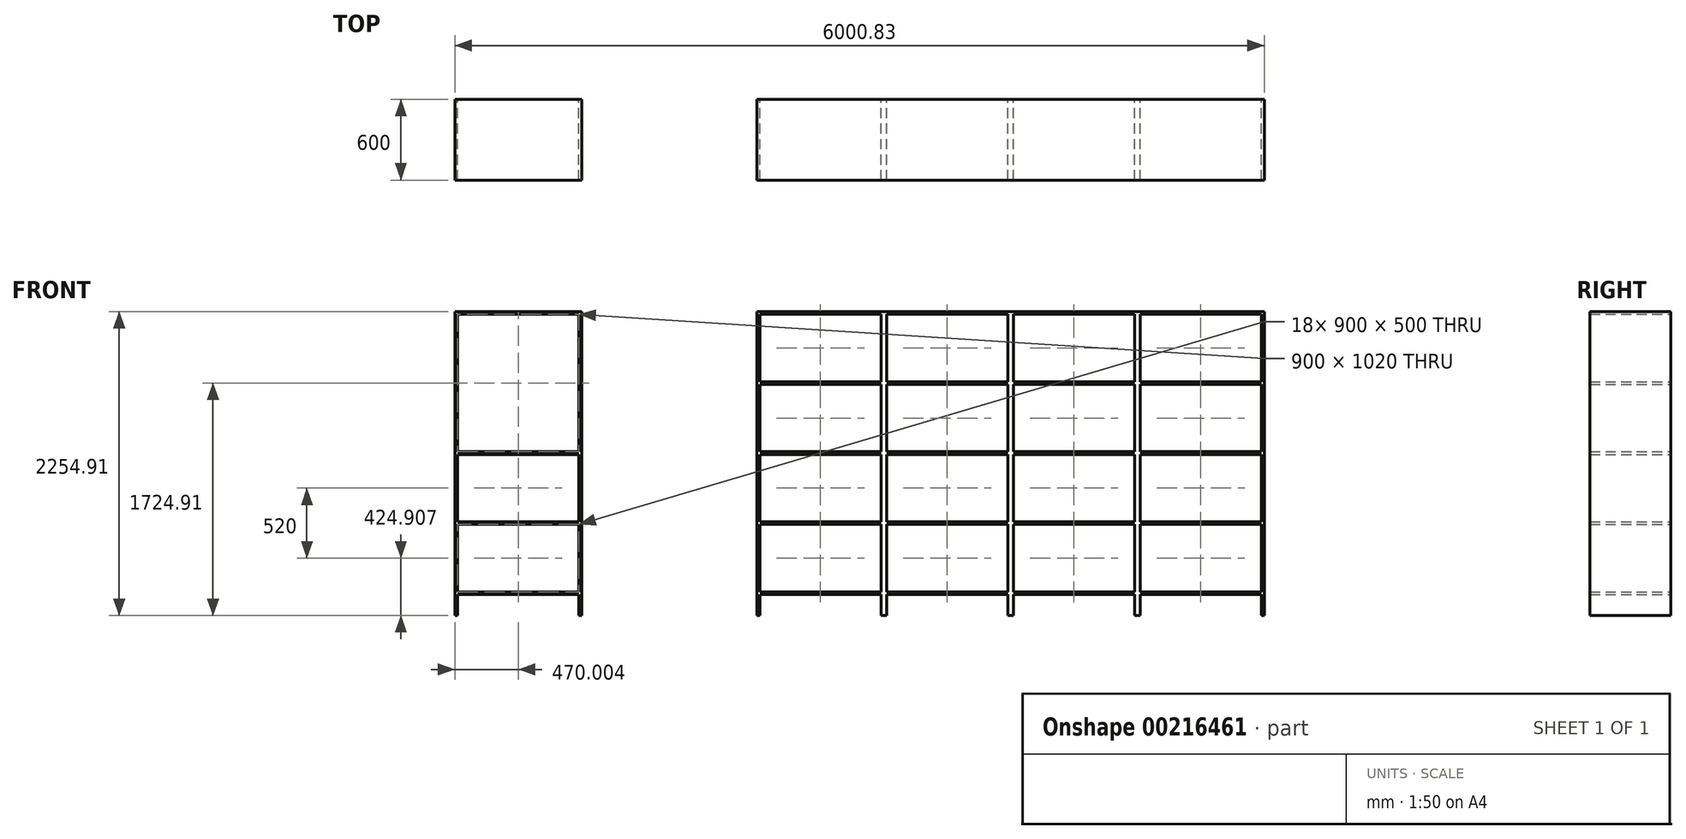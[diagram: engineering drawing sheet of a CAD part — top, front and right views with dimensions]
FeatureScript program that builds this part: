
annotation { "Feature Type Name" : "Feature", "Feature Type Description" : "" }
export const myFeature = defineFeature(function(context is Context, id is Id, definition is map)
    precondition{}
    {
        {
            var Q0;
            Q0=qCreatedBy(makeId("Front.planeOp"),FACE);
            var sketch = newSketch(context, id + "F0", { "sketchPlane" : qUnion([Q0])});
            skLineSegment(sketch, "E0.bottom", {"start": v(0, 842.8) * mm, "end": v(900, 842.8) * mm});
            skLineSegment(sketch, "E0.top", {"start": v(0, 342.8) * mm, "end": v(900, 342.8) * mm});
            skLineSegment(sketch, "E0.left", {"start": v(0, 842.8) * mm, "end": v(0, 342.8) * mm});
            skLineSegment(sketch, "E0.right", {"start": v(900, 842.8) * mm, "end": v(900, 342.8) * mm});
            skLineSegment(sketch, "E1.top", {"start": v(0, 862.8) * mm, "end": v(900, 862.8) * mm});
            skLineSegment(sketch, "E1.left", {"start": v(0, 842.8) * mm, "end": v(0, 862.8) * mm});
            skLineSegment(sketch, "E1.right", {"start": v(900, 842.8) * mm, "end": v(900, 862.8) * mm});
            skLineSegment(sketch, "E2.top", {"start": v(0, 1362.8) * mm, "end": v(900, 1362.8) * mm});
            skLineSegment(sketch, "E2.left", {"start": v(0, 862.8) * mm, "end": v(0, 1362.8) * mm});
            skLineSegment(sketch, "E2.right", {"start": v(900, 862.8) * mm, "end": v(900, 1362.8) * mm});
            skLineSegment(sketch, "E3.top", {"start": v(0, 1382.8) * mm, "end": v(900, 1382.8) * mm});
            skLineSegment(sketch, "E3.left", {"start": v(0, 1362.8) * mm, "end": v(0, 1382.8) * mm});
            skLineSegment(sketch, "E3.right", {"start": v(900, 1362.8) * mm, "end": v(900, 1382.8) * mm});
            skLineSegment(sketch, "E4.top", {"start": v(0, 1882.8) * mm, "end": v(900, 1882.8) * mm});
            skLineSegment(sketch, "E4.left", {"start": v(0, 1382.8) * mm, "end": v(0, 1882.8) * mm});
            skLineSegment(sketch, "E4.right", {"start": v(900, 1382.8) * mm, "end": v(900, 1882.8) * mm});
            skLineSegment(sketch, "E5.top", {"start": v(0, 1902.8) * mm, "end": v(900, 1902.8) * mm});
            skLineSegment(sketch, "E5.left", {"start": v(0, 1882.8) * mm, "end": v(0, 1902.8) * mm});
            skLineSegment(sketch, "E5.right", {"start": v(900, 1882.8) * mm, "end": v(900, 1902.8) * mm});
            skLineSegment(sketch, "E6.top", {"start": v(0, 2402.8) * mm, "end": v(900, 2402.8) * mm});
            skLineSegment(sketch, "E6.left", {"start": v(0, 1902.8) * mm, "end": v(0, 2402.8) * mm});
            skLineSegment(sketch, "E6.right", {"start": v(900, 1902.8) * mm, "end": v(900, 2402.8) * mm});
            skLineSegment(sketch, "E7.bottom", {"start": v(0, 2402.8) * mm, "end": v(-20, 2402.8) * mm});
            skLineSegment(sketch, "E7.top", {"start": v(0, 167.9) * mm, "end": v(-20, 167.9) * mm});
            skLineSegment(sketch, "E7.left", {"start": v(0, 2402.8) * mm, "end": v(0, 167.9) * mm});
            skLineSegment(sketch, "E7.right", {"start": v(-20, 2402.8) * mm, "end": v(-20, 167.9) * mm});
            skLineSegment(sketch, "E8.bottom", {"start": v(900, 2402.8) * mm, "end": v(920, 2402.8) * mm});
            skLineSegment(sketch, "E8.top", {"start": v(900, 167.9) * mm, "end": v(920, 167.9) * mm});
            skLineSegment(sketch, "E8.left", {"start": v(900, 2402.8) * mm, "end": v(900, 167.9) * mm});
            skLineSegment(sketch, "E8.right", {"start": v(920, 2402.8) * mm, "end": v(920, 167.9) * mm});
            skLineSegment(sketch, "E9.bottom", {"start": v(-20, 2402.8) * mm, "end": v(920, 2402.8) * mm});
            skLineSegment(sketch, "E9.top", {"start": v(-20, 2422.8) * mm, "end": v(920, 2422.8) * mm});
            skLineSegment(sketch, "E9.left", {"start": v(-20, 2402.8) * mm, "end": v(-20, 2422.8) * mm});
            skLineSegment(sketch, "E9.right", {"start": v(920, 2402.8) * mm, "end": v(920, 2422.8) * mm});
            skLineSegment(sketch, "E10.bottom", {"start": v(0, 322.8) * mm, "end": v(900, 322.8) * mm});
            skLineSegment(sketch, "E10.left", {"start": v(0, 322.8) * mm, "end": v(0, 342.8) * mm});
            skLineSegment(sketch, "E10.right", {"start": v(900, 322.8) * mm, "end": v(900, 342.8) * mm});
            skLineSegment(sketch, "E11", {"start": v(920, 2626.25) * mm, "end": v(920, 3237.78) * mm, "construction": true});
            skLineSegment(sketch, "E12", {"start": v(-670.41, 2612.4) * mm, "end": v(-670.41, 3024.7) * mm, "construction": true});
            skLineSegment(sketch, "E13.MirrorCS", {"start": v(-2240.83, 1362.8) * mm, "end": v(-2240.83, 1382.8) * mm});
            skLineSegment(sketch, "E14.MirrorCS", {"start": v(-2240.83, 842.8) * mm, "end": v(-2240.83, 862.8) * mm});
            skLineSegment(sketch, "E15.MirrorCS", {"start": v(-1340.83, 842.8) * mm, "end": v(-1340.83, 862.8) * mm});
            skLineSegment(sketch, "E16.MirrorCS", {"start": v(-1340.83, 1362.8) * mm, "end": v(-1340.83, 1382.8) * mm});
            skLineSegment(sketch, "E17.MirrorCS", {"start": v(-1340.83, 322.8) * mm, "end": v(-1340.83, 342.8) * mm});
            skLineSegment(sketch, "E18.MirrorCS", {"start": v(-2240.83, 1882.8) * mm, "end": v(-2240.83, 1902.8) * mm});
            skLineSegment(sketch, "E19.MirrorCS", {"start": v(-1340.83, 1882.8) * mm, "end": v(-1340.83, 1902.8) * mm});
            skLineSegment(sketch, "E20.MirrorCS", {"start": v(-2240.83, 322.8) * mm, "end": v(-2240.83, 342.8) * mm});
            skLineSegment(sketch, "E21.MirrorCS", {"start": v(-1340.83, 167.9) * mm, "end": v(-1320.83, 167.9) * mm});
            skLineSegment(sketch, "E22.MirrorCS", {"start": v(-2240.83, 167.9) * mm, "end": v(-2260.83, 167.9) * mm});
            skLineSegment(sketch, "E23.MirrorCS", {"start": v(-2240.83, 1382.8) * mm, "end": v(-2240.83, 1882.8) * mm});
            skLineSegment(sketch, "E24.MirrorCS", {"start": v(-1340.83, 1882.8) * mm, "end": v(-2240.83, 1882.8) * mm});
            skLineSegment(sketch, "E25.MirrorCS", {"start": v(-2240.83, 862.8) * mm, "end": v(-2240.83, 1362.8) * mm});
            skLineSegment(sketch, "E26.MirrorCS", {"start": v(-1340.83, 1902.8) * mm, "end": v(-2240.83, 1902.8) * mm});
            skLineSegment(sketch, "E27.MirrorCS", {"start": v(-1340.83, 842.8) * mm, "end": v(-1340.83, 342.8) * mm});
            skLineSegment(sketch, "E28.MirrorCS", {"start": v(-1340.83, 1382.8) * mm, "end": v(-2240.83, 1382.8) * mm});
            skLineSegment(sketch, "E29.MirrorCS", {"start": v(-1340.83, 1902.8) * mm, "end": v(-1340.83, 2402.8) * mm});
            skLineSegment(sketch, "E30.MirrorCS", {"start": v(-1340.83, 1362.8) * mm, "end": v(-2240.83, 1362.8) * mm});
            skLineSegment(sketch, "E31.MirrorCS", {"start": v(-1340.83, 862.8) * mm, "end": v(-2240.83, 862.8) * mm});
            skLineSegment(sketch, "E32.MirrorCS", {"start": v(-2240.83, 842.8) * mm, "end": v(-2240.83, 342.8) * mm});
            skLineSegment(sketch, "E33.MirrorCS", {"start": v(-1340.83, 862.8) * mm, "end": v(-1340.83, 1362.8) * mm});
            skLineSegment(sketch, "E34.MirrorCS", {"start": v(-2240.83, 1902.8) * mm, "end": v(-2240.83, 2402.8) * mm});
            skLineSegment(sketch, "E35.MirrorCS", {"start": v(-1340.83, 842.8) * mm, "end": v(-2240.83, 842.8) * mm});
            skLineSegment(sketch, "E36.MirrorCS", {"start": v(-1340.83, 342.8) * mm, "end": v(-2240.83, 342.8) * mm});
            skLineSegment(sketch, "E37.MirrorCS", {"start": v(-1340.83, 322.8) * mm, "end": v(-2240.83, 322.8) * mm});
            skLineSegment(sketch, "E38.MirrorCS", {"start": v(-2260.83, 2402.8) * mm, "end": v(-2260.83, 167.9) * mm});
            skLineSegment(sketch, "E39.MirrorCS", {"start": v(-2240.83, 2402.8) * mm, "end": v(-2240.83, 167.9) * mm});
            skLineSegment(sketch, "E40.MirrorCS", {"start": v(-1320.83, 2402.8) * mm, "end": v(-1320.83, 167.9) * mm});
            skLineSegment(sketch, "E41.MirrorCS", {"start": v(-1340.83, 2402.8) * mm, "end": v(-1340.83, 167.9) * mm});
            skLineSegment(sketch, "E42.MirrorCS", {"start": v(-1340.83, 1382.8) * mm, "end": v(-1340.83, 1882.8) * mm});
            skLineSegment(sketch, "E43.MirrorCS", {"start": v(-1340.83, 2402.8) * mm, "end": v(-2240.83, 2402.8) * mm});
            skLineSegment(sketch, "E44.MirrorCS", {"start": v(-1320.83, 2422.8) * mm, "end": v(-2260.83, 2422.8) * mm});
            skLineSegment(sketch, "E45.MirrorCS", {"start": v(1840, 2402.8) * mm, "end": v(1860, 2402.8) * mm});
            skLineSegment(sketch, "E46.MirrorCS", {"start": v(940, 322.8) * mm, "end": v(940, 342.8) * mm});
            skLineSegment(sketch, "E47.MirrorCS", {"start": v(1840, 1362.8) * mm, "end": v(1840, 1382.8) * mm});
            skLineSegment(sketch, "E48.MirrorCS", {"start": v(940, 1362.8) * mm, "end": v(940, 1382.8) * mm});
            skLineSegment(sketch, "E49.MirrorCS", {"start": v(940, 2402.8) * mm, "end": v(920, 2402.8) * mm});
            skLineSegment(sketch, "E50.MirrorCS", {"start": v(1860, 2402.8) * mm, "end": v(1860, 2422.8) * mm});
            skLineSegment(sketch, "E51.MirrorCS", {"start": v(940, 1882.8) * mm, "end": v(940, 1902.8) * mm});
            skLineSegment(sketch, "E52.MirrorCS", {"start": v(940, 842.8) * mm, "end": v(940, 862.8) * mm});
            skLineSegment(sketch, "E53.MirrorCS", {"start": v(1840, 1882.8) * mm, "end": v(1840, 1902.8) * mm});
            skLineSegment(sketch, "E54.MirrorCS", {"start": v(1840, 322.8) * mm, "end": v(1840, 342.8) * mm});
            skLineSegment(sketch, "E55.MirrorCS", {"start": v(1840, 842.8) * mm, "end": v(1840, 862.8) * mm});
            skLineSegment(sketch, "E56.MirrorCS", {"start": v(1840, 167.9) * mm, "end": v(1860, 167.9) * mm});
            skLineSegment(sketch, "E57.MirrorCS", {"start": v(940, 167.9) * mm, "end": v(920, 167.9) * mm});
            skLineSegment(sketch, "E58.MirrorCS", {"start": v(1840, 842.8) * mm, "end": v(940, 842.8) * mm});
            skLineSegment(sketch, "E59.MirrorCS", {"start": v(1840, 342.8) * mm, "end": v(940, 342.8) * mm});
            skLineSegment(sketch, "E60.MirrorCS", {"start": v(1840, 1902.8) * mm, "end": v(940, 1902.8) * mm});
            skLineSegment(sketch, "E61.MirrorCS", {"start": v(940, 1902.8) * mm, "end": v(940, 2402.8) * mm});
            skLineSegment(sketch, "E62.MirrorCS", {"start": v(1840, 1882.8) * mm, "end": v(940, 1882.8) * mm});
            skLineSegment(sketch, "E63.MirrorCS", {"start": v(1840, 1382.8) * mm, "end": v(940, 1382.8) * mm});
            skLineSegment(sketch, "E64.MirrorCS", {"start": v(1860, 2402.8) * mm, "end": v(920, 2402.8) * mm});
            skLineSegment(sketch, "E65.MirrorCS", {"start": v(1840, 862.8) * mm, "end": v(940, 862.8) * mm});
            skLineSegment(sketch, "E66.MirrorCS", {"start": v(940, 862.8) * mm, "end": v(940, 1362.8) * mm});
            skLineSegment(sketch, "E67.MirrorCS", {"start": v(940, 842.8) * mm, "end": v(940, 342.8) * mm});
            skLineSegment(sketch, "E68.MirrorCS", {"start": v(940, 1382.8) * mm, "end": v(940, 1882.8) * mm});
            skLineSegment(sketch, "E69.MirrorCS", {"start": v(1840, 1362.8) * mm, "end": v(940, 1362.8) * mm});
            skLineSegment(sketch, "E70.MirrorCS", {"start": v(1840, 1902.8) * mm, "end": v(1840, 2402.8) * mm});
            skLineSegment(sketch, "E71.MirrorCS", {"start": v(1840, 2402.8) * mm, "end": v(940, 2402.8) * mm});
            skLineSegment(sketch, "E72.MirrorCS", {"start": v(1840, 1382.8) * mm, "end": v(1840, 1882.8) * mm});
            skLineSegment(sketch, "E73.MirrorCS", {"start": v(940, 2402.8) * mm, "end": v(940, 167.9) * mm});
            skLineSegment(sketch, "E74.MirrorCS", {"start": v(1860, 2422.8) * mm, "end": v(920, 2422.8) * mm});
            skLineSegment(sketch, "E75.MirrorCS", {"start": v(1840, 2402.8) * mm, "end": v(1840, 167.9) * mm});
            skLineSegment(sketch, "E76.MirrorCS", {"start": v(1860, 2402.8) * mm, "end": v(1860, 167.9) * mm});
            skLineSegment(sketch, "E77.MirrorCS", {"start": v(1840, 842.8) * mm, "end": v(1840, 342.8) * mm});
            skLineSegment(sketch, "E78.MirrorCS", {"start": v(1840, 862.8) * mm, "end": v(1840, 1362.8) * mm});
            skLineSegment(sketch, "E79.MirrorCS", {"start": v(1840, 322.8) * mm, "end": v(940, 322.8) * mm});
            skLineSegment(sketch, "E80", {"start": v(1860, 2643.35) * mm, "end": v(1860, 2780.12) * mm, "construction": true});
            skLineSegment(sketch, "E81.MirrorCS", {"start": v(2800, 2402.8) * mm, "end": v(2800, 2422.8) * mm});
            skLineSegment(sketch, "E82.MirrorCS", {"start": v(2780, 2402.8) * mm, "end": v(2800, 2402.8) * mm});
            skLineSegment(sketch, "E83.MirrorCS", {"start": v(2820, 2402.8) * mm, "end": v(2800, 2402.8) * mm});
            skLineSegment(sketch, "E84.MirrorCS", {"start": v(3720, 2402.8) * mm, "end": v(3740, 2402.8) * mm});
            skLineSegment(sketch, "E85.MirrorCS", {"start": v(2780, 167.9) * mm, "end": v(2800, 167.9) * mm});
            skLineSegment(sketch, "E86.MirrorCS", {"start": v(2820, 167.9) * mm, "end": v(2800, 167.9) * mm});
            skLineSegment(sketch, "E87.MirrorCS", {"start": v(1880, 2402.8) * mm, "end": v(1860, 2402.8) * mm});
            skLineSegment(sketch, "E88.MirrorCS", {"start": v(3740, 2402.8) * mm, "end": v(3740, 2422.8) * mm});
            skLineSegment(sketch, "E89.MirrorCS", {"start": v(2780, 1362.8) * mm, "end": v(2780, 1382.8) * mm});
            skLineSegment(sketch, "E90.MirrorCS", {"start": v(1880, 1362.8) * mm, "end": v(1880, 1382.8) * mm});
            skLineSegment(sketch, "E91.MirrorCS", {"start": v(2820, 1882.8) * mm, "end": v(2820, 1902.8) * mm});
            skLineSegment(sketch, "E92.MirrorCS", {"start": v(3720, 322.8) * mm, "end": v(3720, 342.8) * mm});
            skLineSegment(sketch, "E93.MirrorCS", {"start": v(1880, 1882.8) * mm, "end": v(1880, 1902.8) * mm});
            skLineSegment(sketch, "E94.MirrorCS", {"start": v(2780, 842.8) * mm, "end": v(2780, 862.8) * mm});
            skLineSegment(sketch, "E95.MirrorCS", {"start": v(3720, 1362.8) * mm, "end": v(3720, 1382.8) * mm});
            skLineSegment(sketch, "E96.MirrorCS", {"start": v(1880, 322.8) * mm, "end": v(1880, 342.8) * mm});
            skLineSegment(sketch, "E97.MirrorCS", {"start": v(1880, 842.8) * mm, "end": v(1880, 862.8) * mm});
            skLineSegment(sketch, "E98.MirrorCS", {"start": v(2780, 322.8) * mm, "end": v(2780, 342.8) * mm});
            skLineSegment(sketch, "E99.MirrorCS", {"start": v(3720, 1882.8) * mm, "end": v(3720, 1902.8) * mm});
            skLineSegment(sketch, "E100.MirrorCS", {"start": v(2780, 1882.8) * mm, "end": v(2780, 1902.8) * mm});
            skLineSegment(sketch, "E101.MirrorCS", {"start": v(2820, 842.8) * mm, "end": v(2820, 862.8) * mm});
            skLineSegment(sketch, "E102.MirrorCS", {"start": v(2820, 1362.8) * mm, "end": v(2820, 1382.8) * mm});
            skLineSegment(sketch, "E103.MirrorCS", {"start": v(2820, 322.8) * mm, "end": v(2820, 342.8) * mm});
            skLineSegment(sketch, "E104.MirrorCS", {"start": v(3720, 842.8) * mm, "end": v(3720, 862.8) * mm});
            skLineSegment(sketch, "E105.MirrorCS", {"start": v(2820, 1382.8) * mm, "end": v(2820, 1882.8) * mm});
            skLineSegment(sketch, "E106.MirrorCS", {"start": v(1880, 167.9) * mm, "end": v(1860, 167.9) * mm});
            skLineSegment(sketch, "E107.MirrorCS", {"start": v(2800, 2402.8) * mm, "end": v(2800, 167.9) * mm});
            skLineSegment(sketch, "E108.MirrorCS", {"start": v(3740, 2402.8) * mm, "end": v(2800, 2402.8) * mm});
            skLineSegment(sketch, "E109.MirrorCS", {"start": v(2820, 1902.8) * mm, "end": v(2820, 2402.8) * mm});
            skLineSegment(sketch, "E110.MirrorCS", {"start": v(3720, 167.9) * mm, "end": v(3740, 167.9) * mm});
            skLineSegment(sketch, "E111.MirrorCS", {"start": v(1860, 2422.8) * mm, "end": v(2800, 2422.8) * mm});
            skLineSegment(sketch, "E112.MirrorCS", {"start": v(1880, 2402.8) * mm, "end": v(2780, 2402.8) * mm});
            skLineSegment(sketch, "E113.MirrorCS", {"start": v(1880, 1882.8) * mm, "end": v(2780, 1882.8) * mm});
            skLineSegment(sketch, "E114.MirrorCS", {"start": v(2820, 842.8) * mm, "end": v(2820, 342.8) * mm});
            skLineSegment(sketch, "E115.MirrorCS", {"start": v(1880, 862.8) * mm, "end": v(2780, 862.8) * mm});
            skLineSegment(sketch, "E116.MirrorCS", {"start": v(1880, 862.8) * mm, "end": v(1880, 1362.8) * mm});
            skLineSegment(sketch, "E117.MirrorCS", {"start": v(3720, 1902.8) * mm, "end": v(3720, 2402.8) * mm});
            skLineSegment(sketch, "E118.MirrorCS", {"start": v(1880, 842.8) * mm, "end": v(2780, 842.8) * mm});
            skLineSegment(sketch, "E119.MirrorCS", {"start": v(3720, 342.8) * mm, "end": v(2820, 342.8) * mm});
            skLineSegment(sketch, "E120.MirrorCS", {"start": v(3720, 1902.8) * mm, "end": v(2820, 1902.8) * mm});
            skLineSegment(sketch, "E121.MirrorCS", {"start": v(3720, 1382.8) * mm, "end": v(2820, 1382.8) * mm});
            skLineSegment(sketch, "E122.MirrorCS", {"start": v(1880, 1382.8) * mm, "end": v(2780, 1382.8) * mm});
            skLineSegment(sketch, "E123.MirrorCS", {"start": v(3720, 862.8) * mm, "end": v(2820, 862.8) * mm});
            skLineSegment(sketch, "E124.MirrorCS", {"start": v(3740, 2422.8) * mm, "end": v(2800, 2422.8) * mm});
            skLineSegment(sketch, "E125.MirrorCS", {"start": v(3720, 1882.8) * mm, "end": v(2820, 1882.8) * mm});
            skLineSegment(sketch, "E126.MirrorCS", {"start": v(1880, 342.8) * mm, "end": v(2780, 342.8) * mm});
            skLineSegment(sketch, "E127.MirrorCS", {"start": v(1880, 1362.8) * mm, "end": v(2780, 1362.8) * mm});
            skLineSegment(sketch, "E128.MirrorCS", {"start": v(2820, 862.8) * mm, "end": v(2820, 1362.8) * mm});
            skLineSegment(sketch, "E129.MirrorCS", {"start": v(3720, 842.8) * mm, "end": v(2820, 842.8) * mm});
            skLineSegment(sketch, "E130.MirrorCS", {"start": v(3720, 1362.8) * mm, "end": v(2820, 1362.8) * mm});
            skLineSegment(sketch, "E131.MirrorCS", {"start": v(1880, 1902.8) * mm, "end": v(2780, 1902.8) * mm});
            skLineSegment(sketch, "E132.MirrorCS", {"start": v(1880, 1382.8) * mm, "end": v(1880, 1882.8) * mm});
            skLineSegment(sketch, "E133.MirrorCS", {"start": v(2820, 2402.8) * mm, "end": v(2820, 167.9) * mm});
            skLineSegment(sketch, "E134.MirrorCS", {"start": v(3720, 1382.8) * mm, "end": v(3720, 1882.8) * mm});
            skLineSegment(sketch, "E135.MirrorCS", {"start": v(1860, 2402.8) * mm, "end": v(2800, 2402.8) * mm});
            skLineSegment(sketch, "E136.MirrorCS", {"start": v(3720, 2402.8) * mm, "end": v(2820, 2402.8) * mm});
            skLineSegment(sketch, "E137.MirrorCS", {"start": v(3720, 322.8) * mm, "end": v(2820, 322.8) * mm});
            skLineSegment(sketch, "E138.MirrorCS", {"start": v(1880, 842.8) * mm, "end": v(1880, 342.8) * mm});
            skLineSegment(sketch, "E139.MirrorCS", {"start": v(3720, 842.8) * mm, "end": v(3720, 342.8) * mm});
            skLineSegment(sketch, "E140.MirrorCS", {"start": v(2780, 2402.8) * mm, "end": v(2780, 167.9) * mm});
            skLineSegment(sketch, "E141.MirrorCS", {"start": v(2780, 842.8) * mm, "end": v(2780, 342.8) * mm});
            skLineSegment(sketch, "E142.MirrorCS", {"start": v(2780, 1902.8) * mm, "end": v(2780, 2402.8) * mm});
            skLineSegment(sketch, "E143.MirrorCS", {"start": v(1880, 1902.8) * mm, "end": v(1880, 2402.8) * mm});
            skLineSegment(sketch, "E144.MirrorCS", {"start": v(3720, 2402.8) * mm, "end": v(3720, 167.9) * mm});
            skLineSegment(sketch, "E145.MirrorCS", {"start": v(3740, 2402.8) * mm, "end": v(3740, 167.9) * mm});
            skLineSegment(sketch, "E146.MirrorCS", {"start": v(2780, 862.8) * mm, "end": v(2780, 1362.8) * mm});
            skLineSegment(sketch, "E147.MirrorCS", {"start": v(1880, 322.8) * mm, "end": v(2780, 322.8) * mm});
            skLineSegment(sketch, "E148.MirrorCS", {"start": v(2780, 1382.8) * mm, "end": v(2780, 1882.8) * mm});
            skLineSegment(sketch, "E149.MirrorCS", {"start": v(3720, 862.8) * mm, "end": v(3720, 1362.8) * mm});
            skLineSegment(sketch, "E150.MirrorCS", {"start": v(1880, 2402.8) * mm, "end": v(1880, 167.9) * mm});
            skLineSegment(sketch, "E151.MirrorCS", {"start": v(-2260.83, 2402.8) * mm, "end": v(-2260.83, 2422.8) * mm});
            skLineSegment(sketch, "E152.MirrorCS", {"start": v(-1320.83, 2402.8) * mm, "end": v(-1320.83, 2422.8) * mm});
            skSolve(sketch);
        }
        {
            var Q0;
            {var subQ9=sQuery(id+"F0.wireOp",EDGE,"E7.top");Q0=makeQuery(id+"F0.imprint","IMPRINT",FACE,{"disambiguationData":[TD([[makeQuery(id+"F0.imprint","IMPRINT",EDGE,{"derivedFrom":subQ9}),-1.0]])]});}
            var Q1;
            {var subQ6=sQuery(id+"F0.wireOp",EDGE,"E85.MirrorCS");Q1=makeQuery(id+"F0.imprint","IMPRINT",FACE,{"disambiguationData":[TD([[makeQuery(id+"F0.imprint","IMPRINT",EDGE,{"derivedFrom":subQ6}),1.0]])]});}
            var Q2;
            {var subQ3=sQuery(id+"F0.wireOp",EDGE,"E106.MirrorCS");Q2=makeQuery(id+"F0.imprint","IMPRINT",FACE,{"disambiguationData":[TD([[makeQuery(id+"F0.imprint","IMPRINT",EDGE,{"derivedFrom":subQ3}),-1.0]])]});}
            var Q3;
            {var subQ0=sQuery(id+"F0.wireOp",EDGE,"E129.MirrorCS");Q3=makeQuery(id+"F0.imprint","IMPRINT",FACE,{"disambiguationData":[TD([[makeQuery(id+"F0.imprint","IMPRINT",EDGE,{"derivedFrom":subQ0}),-1.0]])]});}
            var Q4;
            {var subQ11=sQuery(id+"F0.wireOp",EDGE,"E8.top");Q4=makeQuery(id+"F0.imprint","IMPRINT",FACE,{"disambiguationData":[TD([[makeQuery(id+"F0.imprint","IMPRINT",EDGE,{"derivedFrom":subQ11}),1.0]])]});}
            var Q5;
            {var subQ0=sQuery(id+"F0.wireOp",EDGE,"E65.MirrorCS");Q5=makeQuery(id+"F0.imprint","IMPRINT",FACE,{"disambiguationData":[TD([[makeQuery(id+"F0.imprint","IMPRINT",EDGE,{"derivedFrom":subQ0}),1.0]])]});}
            var Q6;
            {var subQ0=sQuery(id+"F0.wireOp",EDGE,"E122.MirrorCS");Q6=makeQuery(id+"F0.imprint","IMPRINT",FACE,{"disambiguationData":[TD([[makeQuery(id+"F0.imprint","IMPRINT",EDGE,{"derivedFrom":subQ0}),-1.0]])]});}
            var Q7;
            {var subQ0=sQuery(id+"F0.wireOp",EDGE,"E2.top");Q7=makeQuery(id+"F0.imprint","IMPRINT",FACE,{"disambiguationData":[TD([[makeQuery(id+"F0.imprint","IMPRINT",EDGE,{"derivedFrom":subQ0}),1.0]])]});}
            var Q8;
            {var subQ0=sQuery(id+"F0.wireOp",EDGE,"E0.bottom");Q8=makeQuery(id+"F0.imprint","IMPRINT",FACE,{"disambiguationData":[TD([[makeQuery(id+"F0.imprint","IMPRINT",EDGE,{"derivedFrom":subQ0}),1.0]])]});}
            var Q9;
            {var subQ0=sQuery(id+"F0.wireOp",EDGE,"E121.MirrorCS");Q9=makeQuery(id+"F0.imprint","IMPRINT",FACE,{"disambiguationData":[TD([[makeQuery(id+"F0.imprint","IMPRINT",EDGE,{"derivedFrom":subQ0}),1.0]])]});}
            var Q10;
            {var subQ2=sQuery(id+"F0.wireOp",EDGE,"E115.MirrorCS");Q10=makeQuery(id+"F0.imprint","IMPRINT",FACE,{"disambiguationData":[TD([[makeQuery(id+"F0.imprint","IMPRINT",EDGE,{"derivedFrom":subQ2}),-1.0]])]});}
            var Q11;
            {var subQ0=sQuery(id+"F0.wireOp",EDGE,"E69.MirrorCS");Q11=makeQuery(id+"F0.imprint","IMPRINT",FACE,{"disambiguationData":[TD([[makeQuery(id+"F0.imprint","IMPRINT",EDGE,{"derivedFrom":subQ0}),-1.0]])]});}
            var Q12;
            {var subQ3=sQuery(id+"F0.wireOp",EDGE,"E81.MirrorCS");Q12=makeQuery(id+"F0.imprint","IMPRINT",FACE,{"disambiguationData":[TD([[makeQuery(id+"F0.imprint","IMPRINT",EDGE,{"derivedFrom":subQ3}),1.0]])]});}
            var Q13;
            {var subQ1=sQuery(id+"F0.wireOp",EDGE,"E81.MirrorCS");Q13=makeQuery(id+"F0.imprint","IMPRINT",FACE,{"disambiguationData":[TD([[makeQuery(id+"F0.imprint","IMPRINT",EDGE,{"derivedFrom":subQ1}),-1.0]])]});}
            var Q14;
            {var subQ12=sQuery(id+"F0.wireOp",EDGE,"E57.MirrorCS");Q14=makeQuery(id+"F0.imprint","IMPRINT",FACE,{"disambiguationData":[TD([[makeQuery(id+"F0.imprint","IMPRINT",EDGE,{"derivedFrom":subQ12}),-1.0]])]});}
            var Q15;
            {var subQ3=sQuery(id+"F0.wireOp",EDGE,"E86.MirrorCS");Q15=makeQuery(id+"F0.imprint","IMPRINT",FACE,{"disambiguationData":[TD([[makeQuery(id+"F0.imprint","IMPRINT",EDGE,{"derivedFrom":subQ3}),-1.0]])]});}
            var Q16;
            {var subQ8=sQuery(id+"F0.wireOp",EDGE,"E110.MirrorCS");Q16=makeQuery(id+"F0.imprint","IMPRINT",FACE,{"disambiguationData":[TD([[makeQuery(id+"F0.imprint","IMPRINT",EDGE,{"derivedFrom":subQ8}),1.0]])]});}
            var Q17;
            Q17=makeQuery(id+"F0.imprint","IMPRINT",FACE,{"disambiguationData":[TD([[makeQuery(id+"F0.imprint","IMPRINT",EDGE,{"derivedFrom":sQuery(id+"F0.wireOp",EDGE,"E9.top")}),-1.0]])]});
            var Q18;
            {var subQ2=sQuery(id+"F0.wireOp",EDGE,"E9.right");Q18=makeQuery(id+"F0.imprint","IMPRINT",FACE,{"disambiguationData":[TD([[makeQuery(id+"F0.imprint","IMPRINT",EDGE,{"derivedFrom":subQ2}),-1.0]])]});}
            var Q19;
            {var subQ0=sQuery(id+"F0.wireOp",EDGE,"E59.MirrorCS");Q19=makeQuery(id+"F0.imprint","IMPRINT",FACE,{"disambiguationData":[TD([[makeQuery(id+"F0.imprint","IMPRINT",EDGE,{"derivedFrom":subQ0}),1.0]])]});}
            var Q20;
            {var subQ0=sQuery(id+"F0.wireOp",EDGE,"E119.MirrorCS");Q20=makeQuery(id+"F0.imprint","IMPRINT",FACE,{"disambiguationData":[TD([[makeQuery(id+"F0.imprint","IMPRINT",EDGE,{"derivedFrom":subQ0}),1.0]])]});}
            var Q21;
            {var subQ4=sQuery(id+"F0.wireOp",EDGE,"E56.MirrorCS");Q21=makeQuery(id+"F0.imprint","IMPRINT",FACE,{"disambiguationData":[TD([[makeQuery(id+"F0.imprint","IMPRINT",EDGE,{"derivedFrom":subQ4}),1.0]])]});}
            var Q22;
            {var subQ0=sQuery(id+"F0.wireOp",EDGE,"E126.MirrorCS");Q22=makeQuery(id+"F0.imprint","IMPRINT",FACE,{"disambiguationData":[TD([[makeQuery(id+"F0.imprint","IMPRINT",EDGE,{"derivedFrom":subQ0}),-1.0]])]});}
            var Q23;
            Q23=makeQuery(id+"F0.imprint","IMPRINT",FACE,{"disambiguationData":[TD([[makeQuery(id+"F0.imprint","IMPRINT",EDGE,{"derivedFrom":sQuery(id+"F0.wireOp",EDGE,"E10.bottom")}),1.0]])]});
            var Q24;
            {var subQ0=sQuery(id+"F0.wireOp",EDGE,"E4.top");Q24=makeQuery(id+"F0.imprint","IMPRINT",FACE,{"disambiguationData":[TD([[makeQuery(id+"F0.imprint","IMPRINT",EDGE,{"derivedFrom":subQ0}),1.0]])]});}
            var Q25;
            {var subQ0=sQuery(id+"F0.wireOp",EDGE,"E113.MirrorCS");Q25=makeQuery(id+"F0.imprint","IMPRINT",FACE,{"disambiguationData":[TD([[makeQuery(id+"F0.imprint","IMPRINT",EDGE,{"derivedFrom":subQ0}),1.0]])]});}
            var Q26;
            {var subQ0=sQuery(id+"F0.wireOp",EDGE,"E125.MirrorCS");Q26=makeQuery(id+"F0.imprint","IMPRINT",FACE,{"disambiguationData":[TD([[makeQuery(id+"F0.imprint","IMPRINT",EDGE,{"derivedFrom":subQ0}),-1.0]])]});}
            var Q27;
            {var subQ0=sQuery(id+"F0.wireOp",EDGE,"E60.MirrorCS");Q27=makeQuery(id+"F0.imprint","IMPRINT",FACE,{"disambiguationData":[TD([[makeQuery(id+"F0.imprint","IMPRINT",EDGE,{"derivedFrom":subQ0}),1.0]])]});}
            var Q28;
            {var subQ20=sQuery(id+"F0.wireOp",EDGE,"E21.MirrorCS");Q28=makeQuery(id+"F0.imprint","IMPRINT",FACE,{"disambiguationData":[TD([[makeQuery(id+"F0.imprint","IMPRINT",EDGE,{"derivedFrom":subQ20}),1.0]])]});}
            var Q29;
            {var subQ0=sQuery(id+"F0.wireOp",EDGE,"E37.MirrorCS");Q29=makeQuery(id+"F0.imprint","IMPRINT",FACE,{"disambiguationData":[TD([[makeQuery(id+"F0.imprint","IMPRINT",EDGE,{"derivedFrom":subQ0}),-1.0]])]});}
            var Q30;
            {var subQ0=sQuery(id+"F0.wireOp",EDGE,"E31.MirrorCS");Q30=makeQuery(id+"F0.imprint","IMPRINT",FACE,{"disambiguationData":[TD([[makeQuery(id+"F0.imprint","IMPRINT",EDGE,{"derivedFrom":subQ0}),1.0]])]});}
            var Q31;
            {var subQ0=sQuery(id+"F0.wireOp",EDGE,"E28.MirrorCS");Q31=makeQuery(id+"F0.imprint","IMPRINT",FACE,{"disambiguationData":[TD([[makeQuery(id+"F0.imprint","IMPRINT",EDGE,{"derivedFrom":subQ0}),1.0]])]});}
            var Q32;
            {var subQ0=sQuery(id+"F0.wireOp",EDGE,"E26.MirrorCS");Q32=makeQuery(id+"F0.imprint","IMPRINT",FACE,{"disambiguationData":[TD([[makeQuery(id+"F0.imprint","IMPRINT",EDGE,{"derivedFrom":subQ0}),1.0]])]});}
            extrude(context, id + "F1", {"entities" : qUnion([Q0, Q1, Q2, Q3, Q4, Q5, Q6, Q7, Q8, Q9, Q10, Q11, Q12, Q13, Q14, Q15, Q16, Q17, Q18, Q19, Q20, Q21, Q22, Q23, Q24, Q25, Q26, Q27, Q28, Q29, Q30, Q31, Q32]), "depth" : 600 * mm});
        }
    });
